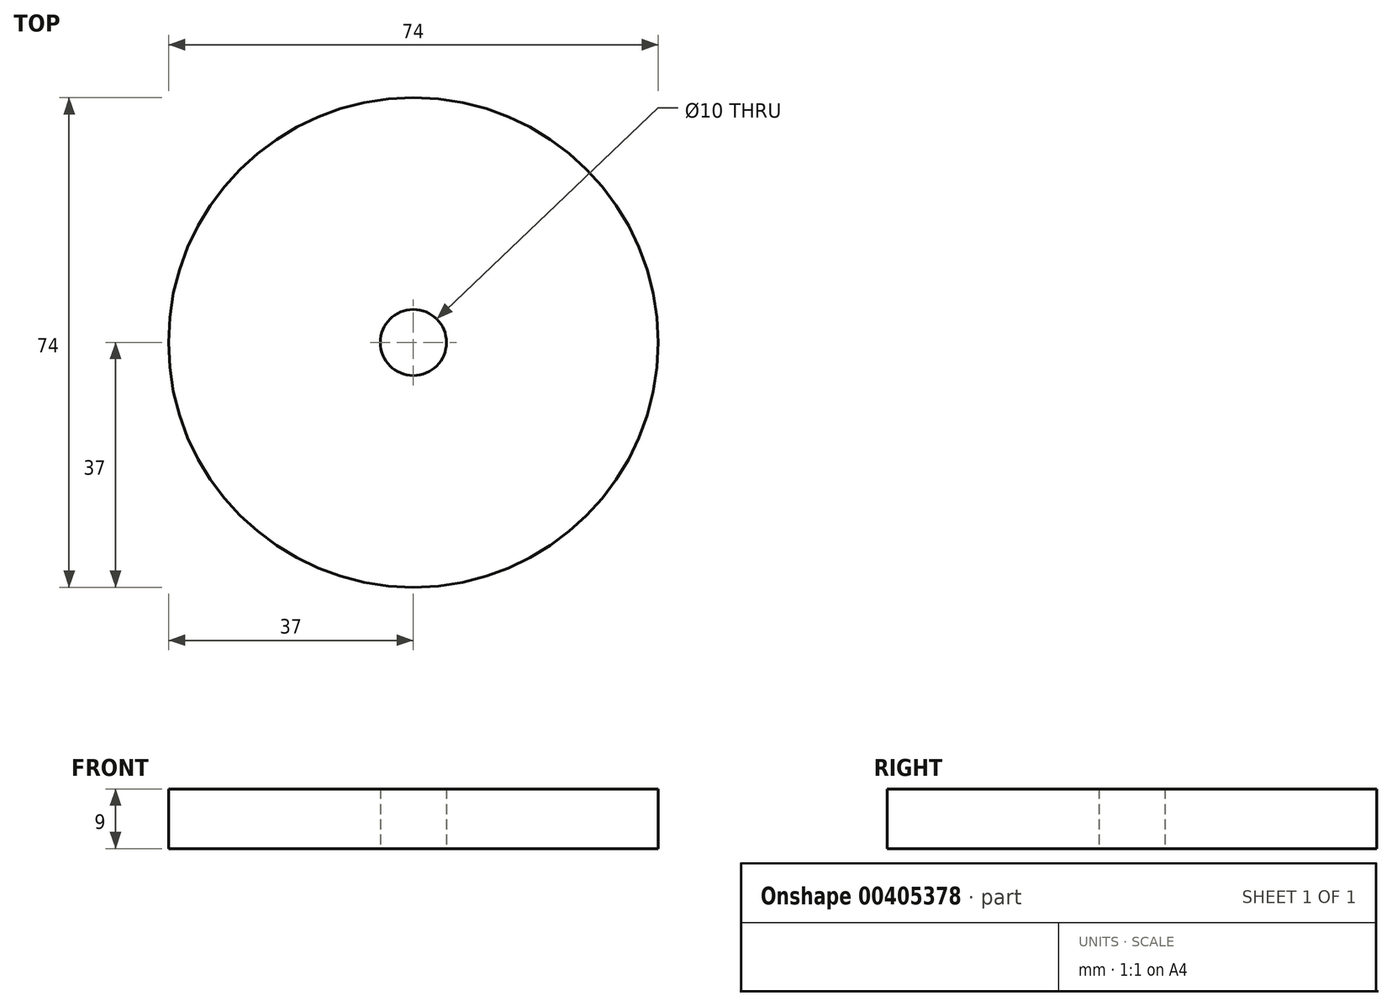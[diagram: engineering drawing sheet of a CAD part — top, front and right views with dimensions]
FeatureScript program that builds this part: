
annotation { "Feature Type Name" : "Feature", "Feature Type Description" : "" }
export const myFeature = defineFeature(function(context is Context, id is Id, definition is map)
    precondition{}
    {
        {
            var Q0;
            Q0=qCreatedBy(makeId("Top.planeOp"),FACE);
            var sketch = newSketch(context, id + "F0", { "sketchPlane" : qUnion([Q0])});
            skCircle(sketch, "E0", {"center": v(0, 0) * mm, "radius": 37 * mm});
            skCircle(sketch, "E1", {"center": v(0, 0) * mm, "radius": 5 * mm});
            skSolve(sketch);
        }
        {
            var Q0;
            Q0=makeQuery(id+"F0.imprint","IMPRINT",FACE,{"disambiguationData":[TD([[makeQuery(id+"F0.imprint","IMPRINT",EDGE,{"derivedFrom":sQuery(id+"F0.wireOp",EDGE,"E0")}),1.0]])]});
            extrude(context, id + "F1", {"entities" : qUnion([Q0]), "depth" : 9 * mm});
        }
    });
